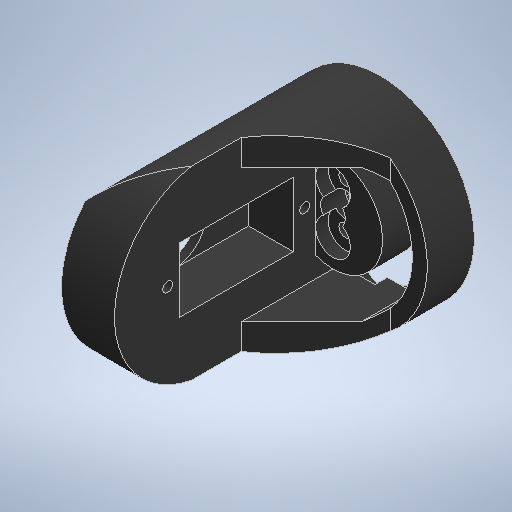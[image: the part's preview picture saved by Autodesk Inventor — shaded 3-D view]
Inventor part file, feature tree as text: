
AUTODESK INVENTOR PART (.ipt)
format: ipt  version: 2025.1 (Build 291241020, 241B)  size: 415,232 bytes
history: native  units: mm
features: extrude x13, sketch x11, mirror x2, chamfer x1, projected_geometry x1
ambient origin geometry x8: Origin, YZ Plane, XZ Plane, XY Plane, X Axis, Y Axis, Z Axis, Center Point
bodies: Body1 (feature_tree)
feature tree (28):
  extrude  "Extrusion28"  Depth=38.0mm
  extrude  "Extrusion34"  Depth=40.5mm
  extrude  "Extrusion35"  Depth=38.0mm
  sketch  "Sketch36"  dims[d258=28.0mm d259=0.0mm d260=0.0mm]
  extrude  "Extrusion36"  TaperAngle=0.0deg  [1 undecoded]
  extrude  "Extrusion37"  Depth=13.0mm
  sketch  "Sketch38"  dims[d261=13.0mm d262=8.0mm]
  extrude  "Extrusion40"  Depth=10.0mm TaperAngle=0.0deg
  extrude  "Extrusion41"  Depth=2.0mm
  extrude  "Extrusion42"  Depth=10.7mm
  extrude  "Extrusion43"  Depth=23.0mm
  extrude  "Extrusion44"  Depth=9.0mm TaperAngle=0.0deg
  mirror  "Mirror2"
  extrude  "Extrusion45"  Depth=2.5mm
  mirror  "Mirror3"
  extrude  "Extrusion46"  Depth=2.5mm
  chamfer  "Chamfer4"  Distance=2.0mm
  extrude  "Extrusion47"  TaperAngle=0.0deg  [1 undecoded]
  sketch  "Sketch30"  dims[d237=50.0mm d238=0.0mm d252=38.0mm]
  sketch  "Sketch33"  dims[d253=14.2mm d254=40.5mm]
  sketch  "Sketch35"  dims[d255=50.0mm d256=0.0mm d257=38.0mm]
  projected_geometry  "Projected Loop6"
  sketch  "Sketch39"  dims[d265=6.5mm d266=10.0mm d267=0.0mm]
  sketch  "Sketch40"  dims[d268=2.0mm d269=0.0mm d271=2.0mm]
  sketch  "Sketch41"  dims[d272=9.0mm d277=10.7mm]
  sketch  "Sketch42"  dims[d278=2.0mm d281=23.0mm]
  sketch  "Sketch43"  dims[d282=13.0mm d284=9.0mm d285=0.0mm]
  sketch  "Sketch44"  dims[d286=2.0mm d287=2.3mm d288=2.3mm d289=2.0mm d290=0.0mm d291=0.0mm d292=32.0mm d293=2.0mm d294=0.0mm d295=20.0mm d296=3.5mm d297=27.0mm d298=0.0mm d299=0.0mm d300=7.0mm d301=14.0mm d302=4.5mm d303=0.0mm d305=10.0mm d306=7.5mm d307=5.5mm d308=2.5mm d309=0.0mm d310=5.0mm d311=2.6mm d312=9.0mm d313=2.5mm d314=0.0mm d315=15.0mm d316=2.0mm d317=45.0deg d318=7.0mm d319=2.5mm d320=0.0mm]
note: 2 required parameter values undecoded (feature->parameter linkage not recoverable at this tier; creation-order binding heuristic only, values carry confidence <= 0.55)
